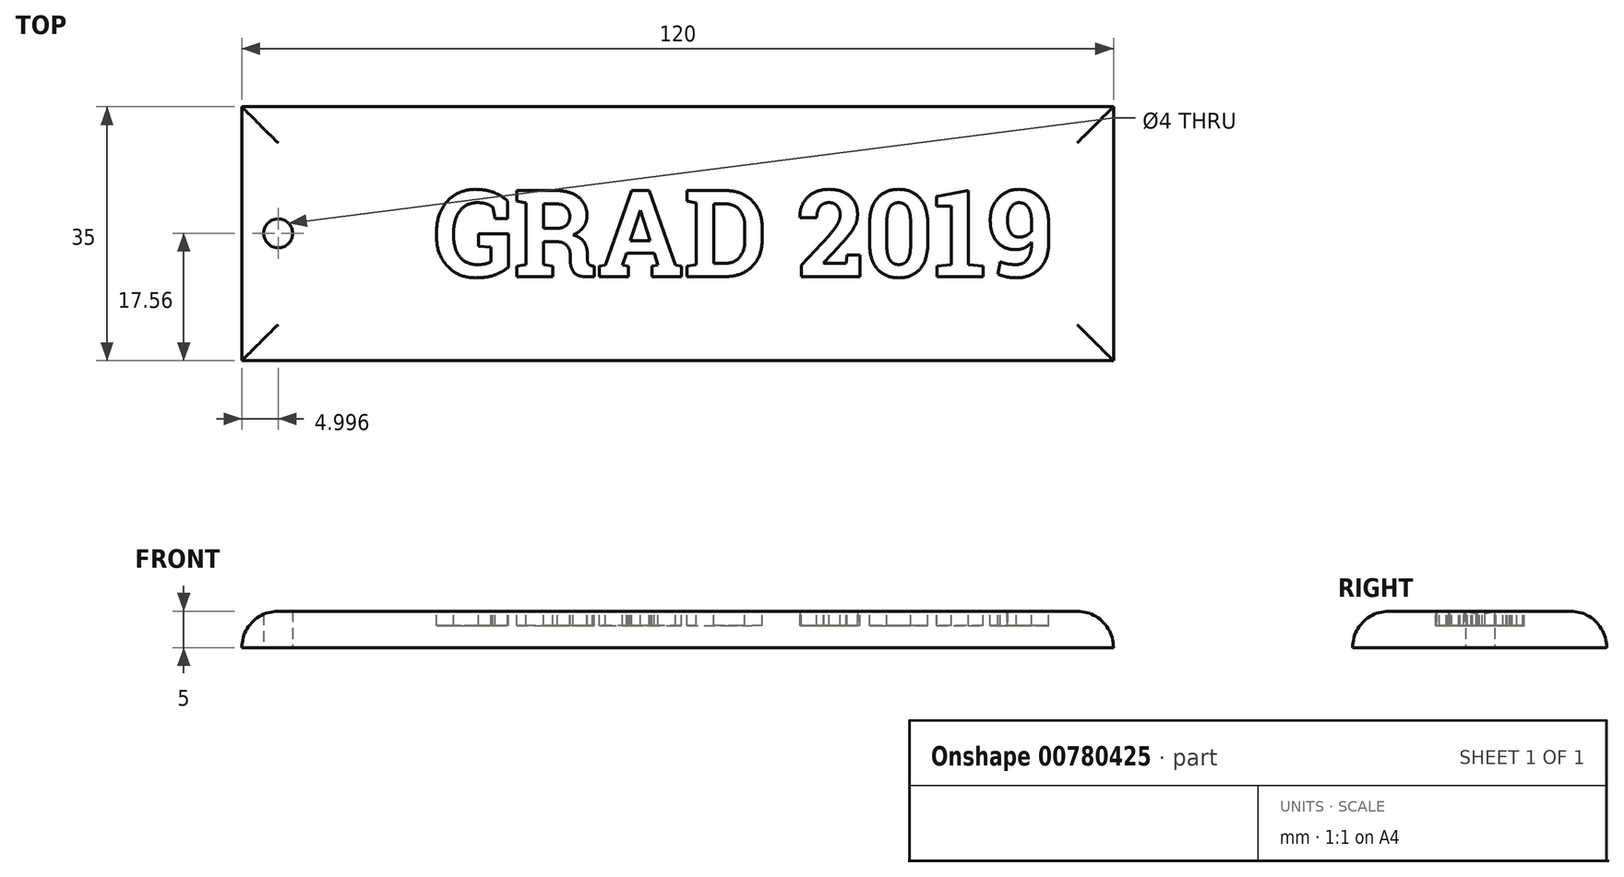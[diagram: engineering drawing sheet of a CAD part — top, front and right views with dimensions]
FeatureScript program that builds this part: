
annotation { "Feature Type Name" : "Feature", "Feature Type Description" : "" }
export const myFeature = defineFeature(function(context is Context, id is Id, definition is map)
    precondition{}
    {
        {
            var Q0;
            Q0=qCreatedBy(makeId("Top.planeOp"),FACE);
            var sketch = newSketch(context, id + "F0", { "sketchPlane" : qUnion([Q0])});
            skLineSegment(sketch, "E0.bottom", {"start": v(63.47, -17.56) * mm, "end": v(-56.53, -17.56) * mm});
            skLineSegment(sketch, "E0.top", {"start": v(63.47, 17.44) * mm, "end": v(-56.53, 17.44) * mm});
            skLineSegment(sketch, "E0.left", {"start": v(63.47, -17.56) * mm, "end": v(63.47, 17.44) * mm});
            skLineSegment(sketch, "E0.right", {"start": v(-56.53, -17.56) * mm, "end": v(-56.53, 17.44) * mm});
            skCircle(sketch, "E1", {"center": v(-51.53, 0) * mm, "radius": 2 * mm});
            skSolve(sketch);
        }
        {
            var Q0;
            Q0=makeQuery(id+"F0.imprint","IMPRINT",FACE,{"disambiguationData":[TD([[makeQuery(id+"F0.imprint","IMPRINT",EDGE,{"derivedFrom":sQuery(id+"F0.wireOp",EDGE,"E0.bottom")}),-1.0]])]});
            extrude(context, id + "F1", {"entities" : qUnion([Q0]), "depth" : 5 * mm, "offsetDistance" : 25 * mm});
        }
        {
            var Q0;
            Q0=makeQuery(id+"F1.opExtrude","CAP_FACE",FACE,{"disambiguationData":[OSD([sQuery(id+"F0.wireOp",EDGE,"E0.bottom"),sQuery(id+"F0.wireOp",EDGE,"E0.top"),sQuery(id+"F0.wireOp",EDGE,"E0.left"),sQuery(id+"F0.wireOp",EDGE,"E0.right"),sQuery(id+"F0.wireOp",EDGE,"E1")])],"isStart":false});
            var sketch = newSketch(context, id + "F2", { "sketchPlane" : qUnion([Q0])});
            skSolve(sketch);
        }
        {
            var Q0;
            Q0=makeQuery(id+"F1.opExtrude","CAP_EDGE",EDGE,{"disambiguationData":[OSD([sQuery(id+"F0.wireOp",EDGE,"E0.right")])],"isStart":false});
            var Q1;
            Q1=makeQuery(id+"F1.opExtrude","CAP_EDGE",EDGE,{"disambiguationData":[OSD([sQuery(id+"F0.wireOp",EDGE,"E0.bottom")])],"isStart":false});
            var Q2;
            Q2=makeQuery(id+"F1.opExtrude","CAP_EDGE",EDGE,{"disambiguationData":[OSD([sQuery(id+"F0.wireOp",EDGE,"E0.left")])],"isStart":false});
            var Q3;
            Q3=makeQuery(id+"F1.opExtrude","CAP_EDGE",EDGE,{"disambiguationData":[OSD([sQuery(id+"F0.wireOp",EDGE,"E0.top")])],"isStart":false});
            fillet(context, id + "F3", {"entities" : qUnion([Q0, Q1, Q2, Q3]), "radius" : 5 * mm, "tangentPropagation" : true, "allowEdgeOverflow" : false});
        }
        {
            var Q0;
            Q0=makeQuery(id+"F2.imprint","IMPRINT",FACE,{"disambiguationData":[TD([[makeQuery(id+"F2.imprint","IMPRINT",EDGE,{"derivedFrom":makeQuery(id+"F1.opExtrude","CAP_EDGE",EDGE,{"disambiguationData":[OSD([sQuery(id+"F0.wireOp",EDGE,"E0.bottom")])],"isStart":false})}),-1.0]])]});
            var sketch = newSketch(context, id + "F4", { "sketchPlane" : qUnion([Q0])});
            skText(sketch, "E2", { "text": "GRAD 2019", "fontName": "RobotoSlab-Bold.ttf"});
            const initialGuessF4  = {"E2": [-0.03012, -0.00596, 1, 0, 0.012]};
            skSetInitialGuess(sketch, initialGuessF4);
            skSolve(sketch);
        }
        {
            var Q0;
            Q0 = qSketchRegion(id + "F4", true);
            extrude(context, id + "F5", {"entities" : qUnion([Q0]), "operationType" : NewBodyOperationType.REMOVE, "oppositeDirection" : true, "depth" : 2 * mm, "offsetDistance" : 25 * mm});
        }
    });
